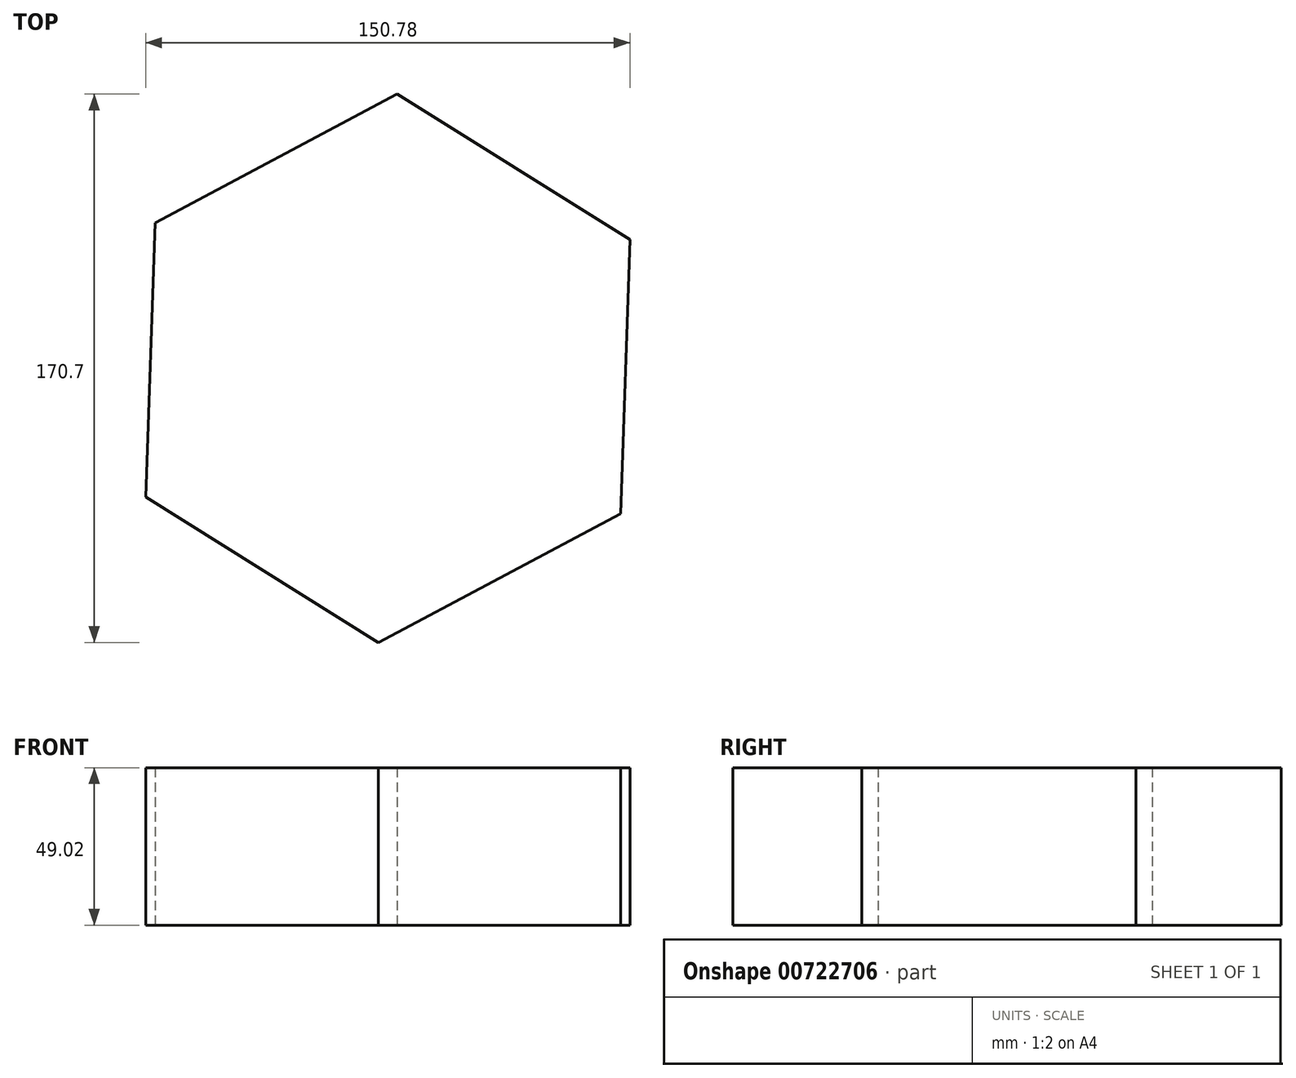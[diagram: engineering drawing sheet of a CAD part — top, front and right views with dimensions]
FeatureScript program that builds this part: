
annotation { "Feature Type Name" : "Feature", "Feature Type Description" : "" }
export const myFeature = defineFeature(function(context is Context, id is Id, definition is map)
    precondition{}
    {
        {
            var Q0;
            Q0=qCreatedBy(makeId("Top.planeOp"),FACE);
            var sketch = newSketch(context, id + "F0", { "sketchPlane" : qUnion([Q0])});
            skCircle(sketch, "E0.cCircle", {"center": v(6.06, 0) * mm, "radius": 73.96 * mm, "construction": true});
            skLineSegment(sketch, "E0.0", {"start": v(-66.38, 45.23) * mm, "end": v(9, 85.35) * mm});
            skLineSegment(sketch, "E0.1", {"start": v(9, 85.35) * mm, "end": v(81.45, 40.12) * mm});
            skLineSegment(sketch, "E0.2", {"start": v(81.45, 40.12) * mm, "end": v(78.5, -45.23) * mm});
            skLineSegment(sketch, "E0.3", {"start": v(78.5, -45.23) * mm, "end": v(3.11, -85.35) * mm});
            skLineSegment(sketch, "E0.4", {"start": v(3.11, -85.35) * mm, "end": v(-69.33, -40.12) * mm});
            skLineSegment(sketch, "E0.5", {"start": v(-69.33, -40.12) * mm, "end": v(-66.38, 45.23) * mm});
            skPoint(sketch, "E0.0.midPoint", {"position": v(-28.69, 65.29) * mm});
            skSolve(sketch);
        }
        {
            var Q0;
            Q0=makeQuery(id+"F0.imprint","IMPRINT",FACE,{"disambiguationData":[TD([[makeQuery(id+"F0.imprint","IMPRINT",EDGE,{"derivedFrom":sQuery(id+"F0.wireOp",EDGE,"E0.0")}),-1.0]])]});
            extrude(context, id + "F1", {"entities" : qUnion([Q0]), "depth" : 49.02 * mm, "offsetDistance" : 25.4 * mm});
        }
    });
